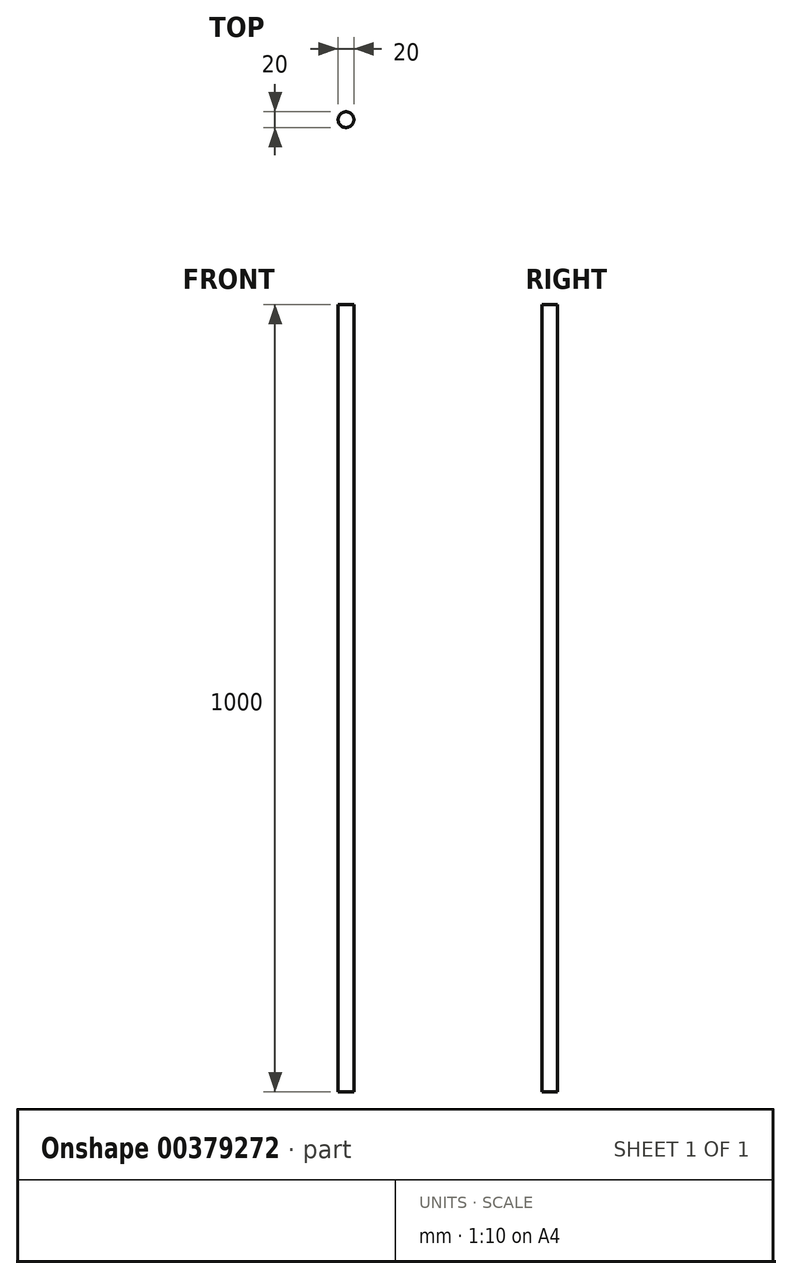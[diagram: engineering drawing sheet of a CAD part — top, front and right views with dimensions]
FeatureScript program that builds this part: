
annotation { "Feature Type Name" : "Feature", "Feature Type Description" : "" }
export const myFeature = defineFeature(function(context is Context, id is Id, definition is map)
    precondition{}
    {
        {
            var Q0;
            Q0=qCreatedBy(makeId("Top.planeOp"),FACE);
            var sketch = newSketch(context, id + "F0", { "sketchPlane" : qUnion([Q0])});
            skCircle(sketch, "E0", {"center": v(0, 0) * mm, "radius": 10 * mm});
            skSolve(sketch);
        }
        {
            var Q0;
            Q0 = qSketchRegion(id + "F0", true);
            extrude(context, id + "F1", {"entities" : qUnion([Q0]), "depth" : 1000 * mm});
        }
    });
